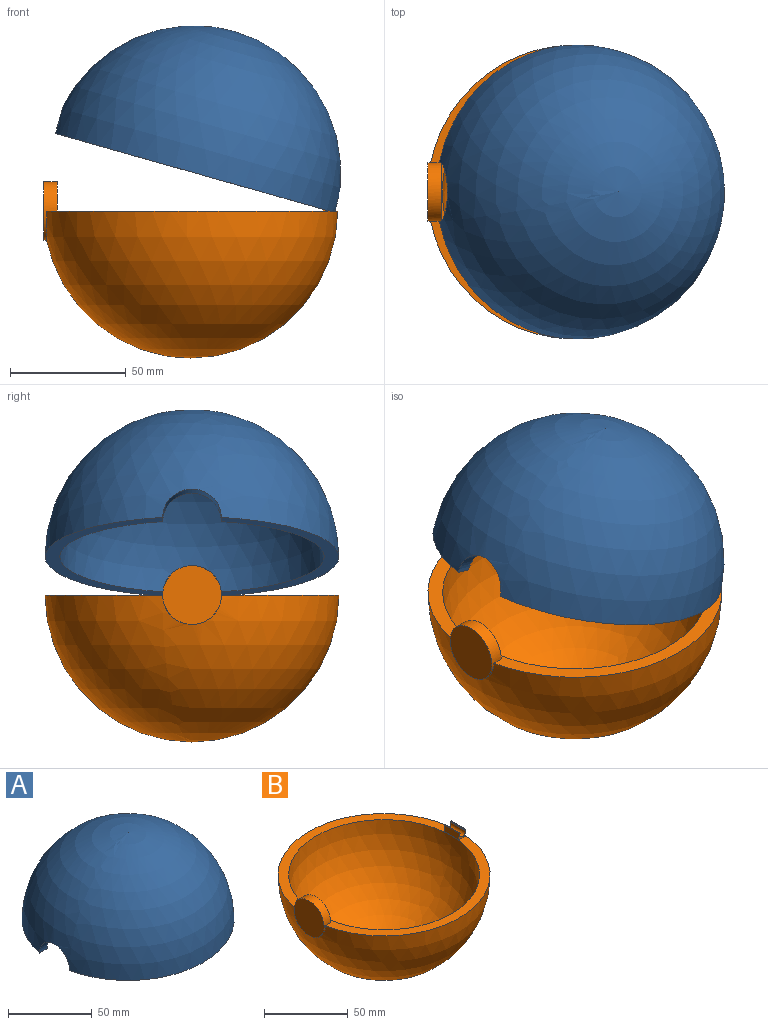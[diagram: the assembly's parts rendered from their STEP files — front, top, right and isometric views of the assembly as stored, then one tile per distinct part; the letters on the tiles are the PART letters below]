
ASSEMBLY  parts=2 mates=1
PART A: 9 faces, bbox 127x127x63.5 mm
  f0: sphere r=57.15mm, area 20184mm2, adj f2,f3,f4,f6,f7,f8
  f1: sphere r=63.5mm, area 24998.5mm2, adj f2,f3,f4,f6,f7,f8
  f2: plane 125.4x57.15mm, normal (0,0,-1), area 1081.8mm2, adj f0,f1,f6,f8
  f3: plane 125.4x57.15mm, normal (0,0,-1), area 1081.8mm2, adj f0,f1,f7,f8
  f4: plane 12.7x6.74mm, normal (0,0,-1), area 81.2mm2, adj f0,f1,f6,f7
  f5: cylinder r=2.29mm len=12.7mm, axis (0,-1,0), area 182.4mm2, adj f6,f7
  f6: plane 6.76x6.37mm, normal (0,-1,0), area 24.2mm2, adj f0,f1,f2,f4,f5
  f7: plane 6.76x6.37mm, normal (0,1,0), area 24.2mm2, adj f0,f1,f3,f4,f5
  f8: cylinder r=12.7mm len=25.4mm, axis (-1,0,0), area 259.2mm2, adj f0,f1,f2,f3
PART B: 17 faces, bbox 127x127x76.2 mm
  f0: plane 127x125.72mm, normal (0,0,1), area 2203mm2, adj f1,f2,f7,f8,f12,f13,f14,f15
  f1: sphere r=63.5mm, area 25079.4mm2, adj f0,f15
  f2: sphere r=57.15mm, area 20521.7mm2, adj f0
  f3: cylinder r=2.29mm len=12.19mm, axis (0,1,0), area 114.6mm2, adj f4,f11,f12,f13
  f4: cylinder r=0.25mm len=12.19mm, axis (0,1,0), area 4.7mm2, adj f3,f5,f12,f13
  f5: plane 12.19x0.37mm, normal (0.47,0,0.88), area 5.1mm2, adj f4,f6,f12,f13
  f6: cylinder r=0.14mm len=12.19mm, axis (0,1,0), area 3.4mm2, adj f5,f7,f12,f13
  f7: plane 12.19x4.57mm, normal (-1,0,0.09), area 55.9mm2, adj f0,f6,f12,f13
  f8: plane 12.19x4.87mm, normal (1,0,-0.08), area 59.6mm2, adj f0,f9,f12,f13
  f9: cylinder r=0.14mm len=12.19mm, axis (0,1,0), area 3.6mm2, adj f8,f10,f12,f13
  f10: plane 12.19x0.33mm, normal (-0.41,0,0.91), area 4.4mm2, adj f9,f11,f12,f13
  f11: cylinder r=0.38mm len=12.19mm, axis (0,1,0), area 7.8mm2, adj f3,f10,f12,f13
  f12: plane 5.86x5.03mm, normal (0,-1,0), area 10.8mm2, adj f0,f3,f4,f5,f6,f7,f8,f9
  f13: plane 5.86x5.03mm, normal (0,1,0), area 10.8mm2, adj f0,f3,f4,f5,f6,f7,f8,f9
  f14: plane 25.4x12.7mm, normal (1,0,0), area 253.4mm2, adj f0,f15
  f15: cylinder r=12.7mm len=25.4mm, axis (-1,0,0), area 284.3mm2, adj f0,f1,f14,f16
  f16: plane 25.4x25.4mm, normal (-1,0,0), area 506.7mm2, adj f15
PLACE A rot(axis=(0,1,0),15.8deg) t=(64.92,0,16.56)mm
PLACE B t=(63.5,0,0)mm
MATE revolute B.f3 <-> A.f5  axis (0,1,0) through (123.82,0,3.17)mm
